# Revit family: 36-90-285-DN65-400
name_source: partatom
category: Pipe Accessories
units: mm (PartAtom-declared; Revit-internal decimal feet)

## family parameters
Always vertical = No
Cut with Voids When Loaded = No
Part Type = Valve - Breaks Into
Round Connector Dimension = Use Diameter
Shared = No
Work Plane-Based = No

## types (13) — shared parameters
Body_Wallthickness = 5 mm  [stored 0.0164042 ft]
DN 065 = Yes
DN 080 = Yes
DN 100 = Yes
DN 125 = Yes
DN 150-160 = Yes
DN 150-180 = Yes
DN 200-200 = Yes
DN 200-225 = Yes
DN 250-250 = Yes
DN 250-280 = Yes
DN 300-315 = Yes
DN 300-355 = Yes
DN 400 = Yes
DN065 = 36-075-88-701084
DN080 = 36-090-88-701084
DN100 = 36-110-88-701084
DN125 = 36-125-88-701084
DN150-160 = 36-160-88-701084
DN200-200 = 36-200-88-701084
DN200-225 = 36-225-88-701084
DN250-280 = 36-280-88-701084
DN300-315 = 36-315-88-701084
DN300-355 = 36-355-88-701084
Description_ = AVK_GATE_VALVE,PE PIPE ENDS
Name_Height_reference = 10 mm  [stored 0.0328084 ft]
Rib_Thickness = 18 mm  [stored 0.0590551 ft]
Search_table = 36-90-285-DN65-400
URL product pages = https://www.avkvalves.com
zero-valued in all types: Bottom_Reference

## per-type parameters (varying)
- DN 065: At=54.5 mm; Body_Height=115 mm; Body_Length=170 mm; Body_depth=109 mm; Body_width=60 mm; Bonnet_Flange_Depth=135 mm; Bonnet_Flange_Width=76 mm; Bonnet_Flange_cut=7.5 mm  [stored 0.0246063 ft]; Bonnet_Flange_thickness=15 mm  [stored 0.0492126 ft]; Bonnet_Height=46.5 mm; Bonnet_Reference_height=105 mm; Bonnet_Thickness=61.2 mm; Bt=61.2 mm; Bt_2=54 mm; CL _Thickness=19 mm  [stored 0.062336 ft]; CL_Height_2=59.5 mm; CL_Thickness 2=21.5 mm  [stored 0.0705381 ft]; Cut_Reference=340 mm; Cut_ref=1350 mm; D=37.5 mm  [stored 0.123031 ft]; D2=44 mm; DN150-180=36-180-88-701084; DN250-250=36-250-88-701084; DN400=36-400-88-701084; F=8.5 mm  [stored 0.0278871 ft]; F1=10 mm  [stored 0.0328084 ft]; F2=34 mm  [stored 0.111549 ft]; F_OD=51 mm; Fillet_Thickness=6 mm  [stored 0.019685 ft]; Flange_OR=39.5 mm; Flange_Thickness=19 mm  [stored 0.062336 ft]; H=271 mm; H3=322 mm; Horizontal_Flange_width=102 mm; ID=32.5 mm  [stored 0.106627 ft]; ID (Radius)=32.5 mm  [stored 0.106627 ft]; L=900 mm; L1=250 mm; L2=400 mm; L_Dia=65 mm; Length=900 mm; Name_Reference=95.833 mm; Name_Width=30 mm  [stored 0.0984252 ft]; Neck_H=62.5 mm; Neck_T=17 mm  [stored 0.0557743 ft]; Neck_T2=15 mm  [stored 0.0492126 ft]; Nominal Diameter (DN)=65 mm; R1tv=930 mm; R2f=15 mm  [stored 0.0492126 ft]; Rf=170 mm; Rib_Height_Reference_1=120 mm; Rib_Height_Reference_2=110 mm; Rib_Height_Reference_3=100 mm; Rib_Height_Reference_4=75 mm; Rib_Width_1=30 mm  [stored 0.0984252 ft]; Rib_Width_2=30 mm  [stored 0.0984252 ft]; Rib_Width_3=30 mm  [stored 0.0984252 ft]; Rib_depth_1=30 mm  [stored 0.0984252 ft]; Rib_depth_2=30 mm  [stored 0.0984252 ft]; Rib_depth_3=30 mm  [stored 0.0984252 ft]; Rt=310 mm
- DN 080: At=62.5 mm; Body_Height=136 mm; Body_Length=180 mm; Body_depth=125 mm; Body_width=72 mm; Bonnet_Flange_Depth=150 mm; Bonnet_Flange_Width=87 mm; Bonnet_Flange_cut=7.5 mm  [stored 0.0246063 ft]; Bonnet_Flange_thickness=15 mm  [stored 0.0492126 ft]; Bonnet_Height=50 mm; Bonnet_Reference_height=126 mm; Bonnet_Thickness=73.44 mm; Bt=73.44 mm; Bt_2=66 mm; CL _Thickness=25 mm  [stored 0.082021 ft]; CL_Height_2=67.5 mm; CL_Thickness 2=27.5 mm  [stored 0.0902231 ft]; Cut_Reference=360 mm; Cut_ref=1350 mm; D=45 mm; D2=50 mm; DN150-180=36-180-88-701084; DN250-250=36-250-88-701084; DN400=36-400-88-701084; F=8.5 mm  [stored 0.0278871 ft]; F1=10 mm  [stored 0.0328084 ft]; F2=34 mm  [stored 0.111549 ft]; F_OD=54 mm; Fillet_Thickness=6 mm  [stored 0.019685 ft]; Flange_OR=47.5 mm; Flange_Thickness=19 mm  [stored 0.062336 ft]; H=297 mm; H3=351 mm; Horizontal_Flange_width=108 mm; ID=40 mm; ID (Radius)=40 mm; L=900 mm; L1=255 mm; L2=390 mm; L_Dia=80 mm; Length=900 mm; Name_Reference=113.333 mm; Name_Width=36 mm  [stored 0.11811 ft]; Neck_H=59.5 mm; Neck_T=23 mm  [stored 0.0754593 ft]; Neck_T2=21 mm; Nominal Diameter (DN)=80 mm; R1tv=1000 mm; R2f=15 mm  [stored 0.0492126 ft]; Rf=180 mm; Rib_Height_Reference_1=120 mm; Rib_Height_Reference_2=110 mm; Rib_Height_Reference_3=100 mm; Rib_Height_Reference_4=85 mm; Rib_Width_1=36 mm  [stored 0.11811 ft]; Rib_Width_2=36 mm  [stored 0.11811 ft]; Rib_Width_3=36 mm  [stored 0.11811 ft]; Rib_depth_1=36 mm  [stored 0.11811 ft]; Rib_depth_2=36 mm  [stored 0.11811 ft]; Rib_depth_3=36 mm  [stored 0.11811 ft]; Rt=333.333 mm
- DN 100: At=77.5 mm; Body_Height=148 mm; Body_Length=190 mm; Body_depth=155 mm; Body_width=81 mm; Bonnet_Flange_Depth=180 mm; Bonnet_Flange_Width=112 mm; Bonnet_Flange_cut=7.5 mm  [stored 0.0246063 ft]; Bonnet_Flange_thickness=15 mm  [stored 0.0492126 ft]; Bonnet_Height=55 mm; Bonnet_Reference_height=138 mm; Bonnet_Thickness=82.62 mm; Bt=82.62 mm; Bt_2=75 mm; CL _Thickness=29.5 mm  [stored 0.0967848 ft]; CL_Height_2=82.5 mm; CL_Thickness 2=32 mm  [stored 0.104987 ft]; Cut_Reference=380 mm; Cut_ref=1290 mm; D=55 mm; D2=64 mm; DN150-180=36-180-88-701084; DN250-250=36-250-88-701084; DN400=36-400-88-701084; F=9.5 mm  [stored 0.031168 ft]; F1=11 mm  [stored 0.0360892 ft]; F2=38 mm  [stored 0.124672 ft]; F_OD=67 mm; Fillet_Thickness=6 mm  [stored 0.019685 ft]; Flange_OR=57.5 mm; Flange_Thickness=100 mm; H=334 mm; H3=401 mm; Horizontal_Flange_width=134 mm; ID=50 mm; ID (Radius)=50 mm; L=860 mm; L1=265 mm; L2=330 mm; L_Dia=100 mm; Length=860 mm; Name_Reference=123.333 mm; Name_Width=40.5 mm; Neck_H=65.5 mm; Neck_T=27.5 mm  [stored 0.0902231 ft]; Neck_T2=25.5 mm  [stored 0.0836614 ft]; Nominal Diameter (DN)=100 mm; R1tv=1100 mm; R2f=15 mm  [stored 0.0492126 ft]; Rf=223.333 mm; Rib_Height_Reference_1=120 mm; Rib_Height_Reference_2=110 mm; Rib_Height_Reference_3=100 mm; Rib_Height_Reference_4=90 mm; Rib_Width_1=40.5 mm; Rib_Width_2=40.5 mm; Rib_Width_3=40.5 mm; Rib_depth_1=40.5 mm; Rib_depth_2=40.5 mm; Rib_depth_3=40.5 mm; Rt=366.667 mm
- DN 150-160: At=113 mm; Body_Height=205 mm; Body_Length=191 mm; Body_depth=226 mm; Body_width=96 mm; Bonnet_Flange_Depth=250 mm; Bonnet_Flange_Width=130 mm; Bonnet_Flange_cut=7.5 mm  [stored 0.0246063 ft]; Bonnet_Flange_thickness=15 mm  [stored 0.0492126 ft]; Bonnet_Height=71 mm; Bonnet_Reference_height=195 mm; Bonnet_Thickness=97.92 mm; Bt=97.92 mm; Bt_2=90 mm; CL _Thickness=34 mm  [stored 0.111549 ft]; CL_Height_2=118 mm; CL_Thickness 2=36.5 mm  [stored 0.119751 ft]; Cut_Reference=382 mm; Cut_ref=1605 mm; D=80 mm; D2=83 mm; DN150-180=36-180-88-701084; DN250-250=36-250-88-701084; DN400=36-400-88-701084
36-400-88-701084; F=9.5 mm  [stored 0.031168 ft]; F1=11 mm  [stored 0.0360892 ft]; F2=38 mm  [stored 0.124672 ft]; F_OD=97 mm; Fillet_Thickness=12 mm  [stored 0.0393701 ft]; Flange_OR=77.5 mm; Flange_Thickness=19 mm  [stored 0.062336 ft]; H=448 mm; H3=545 mm; Horizontal_Flange_width=194 mm; ID=75 mm; ID (Radius)=75.08 mm; L=1070 mm; L1=265 mm; L2=540 mm; L_Dia=150.16 mm; Length=1070 mm; Name_Reference=170.833 mm; Name_Width=48 mm; Neck_H=87 mm; Neck_T=32 mm  [stored 0.104987 ft]; Neck_T2=30 mm  [stored 0.0984252 ft]; Nominal Diameter (DN)=150.16 mm; R1tv=1420 mm; R2f=30 mm  [stored 0.0984252 ft]; Rf=323.333 mm; Rib_Height_Reference_1=120 mm; Rib_Height_Reference_2=110 mm; Rib_Height_Reference_3=100 mm; Rib_Height_Reference_4=150 mm; Rib_Width_1=48 mm; Rib_Width_2=48 mm; Rib_Width_3=48 mm; Rib_depth_1=48 mm; Rib_depth_2=48 mm; Rib_depth_3=48 mm; Rt=473.333 mm
- DN 200-200: At=128.5 mm; Body_Height=289 mm; Body_Length=200 mm; Body_depth=257 mm; Body_width=116 mm; Bonnet_Flange_Depth=283 mm; Bonnet_Flange_Width=150 mm; Bonnet_Flange_cut=12.5 mm  [stored 0.0410105 ft]; Bonnet_Flange_thickness=25 mm  [stored 0.082021 ft]; Bonnet_Height=85 mm; Bonnet_Reference_height=279 mm; Bonnet_Thickness=118.32 mm; Bt=118.32 mm; Bt_2=110 mm; CL _Thickness=38 mm  [stored 0.124672 ft]; CL_Height_2=133.5 mm; CL_Thickness 2=40.5 mm; Cut_Reference=400 mm; Cut_ref=1500 mm; D=100 mm; D2=106 mm; DN150-180=36-180-88-701084; DN250-250=36-250-88-701084; DN400=36-400-88-701084; F=12 mm  [stored 0.0393701 ft]; F1=13.5 mm  [stored 0.0442913 ft]; F2=42 mm; F_OD=115 mm; Fillet_Thickness=24 mm  [stored 0.0787402 ft]; Flange_OR=110 mm; Flange_Thickness=20 mm  [stored 0.0656168 ft]; H=562 mm; H3=677 mm; Horizontal_Flange_width=230 mm; ID=90 mm; ID (Radius)=100.1 mm; L=1000 mm; L1=300 mm; L2=400 mm; L_Dia=200.2 mm; Length=1000 mm; Name_Reference=240.833 mm; Name_Width=58 mm; Neck_H=97.5 mm; Neck_T=36 mm  [stored 0.11811 ft]; Neck_T2=34 mm  [stored 0.111549 ft]; Nominal Diameter (DN)=200.2 mm; R1tv=1700 mm; R2f=60 mm; Rf=383.333 mm; Rib_Height_Reference_1=120 mm; Rib_Height_Reference_2=110 mm; Rib_Height_Reference_3=100 mm; Rib_Height_Reference_4=180 mm; Rib_Width_1=58 mm; Rib_Width_2=58 mm; Rib_Width_3=58 mm; Rib_depth_1=58 mm; Rib_depth_2=58 mm; Rib_depth_3=58 mm; Rt=566.667 mm
- DN 250-250: At=164.5 mm; Body_Height=305 mm; Body_Length=242 mm; Body_depth=329 mm; Body_width=112 mm; Bonnet_Flange_Depth=372 mm; Bonnet_Flange_Width=144 mm; Bonnet_Flange_cut=12.5 mm  [stored 0.0410105 ft]; Bonnet_Flange_thickness=25 mm  [stored 0.082021 ft]; Bonnet_Height=97.5 mm; Bonnet_Reference_height=295 mm; Bonnet_Thickness=114.24 mm; Bt=114.24 mm; Bt_2=106 mm; CL _Thickness=36 mm  [stored 0.11811 ft]; CL_Height_2=169.5 mm; CL_Thickness 2=38.5 mm; Cut_Reference=484 mm; Cut_ref=1920 mm; D=125 mm; D2=109 mm; DN150-180=36-200-88-701084; DN250-250=36-250-88-701084; DN400=36-400-88-701084; F=13.5 mm  [stored 0.0442913 ft]; F1=15.5 mm  [stored 0.050853 ft]; F2=47 mm; F_OD=146 mm; Fillet_Thickness=24 mm  [stored 0.0787402 ft]; Flange_OR=127.5 mm; Flange_Thickness=22 mm  [stored 0.0721785 ft]; H=664 mm; H3=810 mm; Horizontal_Flange_width=292 mm; ID=115 mm; ID (Radius)=125.125 mm; L=1280 mm; L1=270 mm; L2=740 mm; L_Dia=250.25 mm; Length=1280 mm; Name_Reference=254.167 mm; Name_Width=56 mm; Neck_H=142.5 mm; Neck_T=34 mm  [stored 0.111549 ft]; Neck_T2=32 mm  [stored 0.104987 ft]; Nominal Diameter (DN)=250.25 mm; R1tv=1950 mm; R2f=60 mm; Rf=486.667 mm; Rib_Height_Reference_1=90 mm; Rib_Height_Reference_2=110 mm; Rib_Height_Reference_3=100 mm; Rib_Height_Reference_4=200 mm; Rib_Width_1=126 mm; Rib_Width_2=56 mm; Rib_Width_3=56 mm; Rib_depth_1=385 mm; Rib_depth_2=56 mm; Rib_depth_3=56 mm; Rt=650 mm
- DN 300-315: At=209 mm; Body_Height=370 mm; Body_Length=284 mm; Body_depth=418 mm; Body_width=129 mm; Bonnet_Flange_Depth=448 mm; Bonnet_Flange_Width=172 mm; Bonnet_Flange_cut=17.5 mm  [stored 0.0574147 ft]; Bonnet_Flange_thickness=35 mm  [stored 0.114829 ft]; Bonnet_Height=114 mm; Bonnet_Reference_height=360 mm; Bonnet_Thickness=131.58 mm; Bt=131.58 mm; Bt_2=123 mm; CL _Thickness=44.5 mm; CL_Height_2=214 mm; CL_Thickness 2=47 mm; Cut_Reference=568 mm; Cut_ref=2130 mm; D=157.5 mm; D2=110 mm; DN150-180=36-180-88-701084; DN250-250=36-250-88-701084; DN400=36-400-88-701084; F=13.5 mm  [stored 0.0442913 ft]; F1=15.5 mm  [stored 0.050853 ft]; F2=47 mm; F_OD=184 mm; Fillet_Thickness=24 mm  [stored 0.0787402 ft]; Flange_OR=161 mm; Flange_Thickness=24.5 mm  [stored 0.0803806 ft]; H=740 mm; H3=924 mm; Horizontal_Flange_width=368 mm; ID=150 mm; ID (Radius)=150.158 mm; L=1420 mm; L1=265 mm; L2=890 mm; L_Dia=300.315 mm; Length=1420 mm; Name_Reference=308.333 mm; Name_Width=64.5 mm; Neck_H=109 mm; Neck_T=42.5 mm; Neck_T2=40.5 mm; Nominal Diameter (DN)=300.315 mm; R1tv=2280 mm; R2f=60 mm; Rf=613.333 mm; Rib_Height_Reference_1=240 mm; Rib_Height_Reference_2=285 mm; Rib_Height_Reference_3=130 mm; Rib_Height_Reference_4=260 mm; Rib_Width_1=155 mm; Rib_Width_2=155 mm; Rib_Width_3=64.5 mm; Rib_depth_1=456 mm; Rib_depth_2=456 mm; Rib_depth_3=64.5 mm; Rt=760 mm
- DN 400: At=238 mm; Body_Height=485 mm; Body_Length=290 mm; Body_depth=476 mm; Body_width=150 mm; Bonnet_Flange_Depth=554 mm; Bonnet_Flange_Width=178 mm; Bonnet_Flange_cut=35 mm  [stored 0.114829 ft]; Bonnet_Flange_thickness=70 mm; Bonnet_Height=145 mm; Bonnet_Reference_height=475 mm; Bonnet_Thickness=153 mm; Bt=153 mm; Bt_2=144 mm; CL _Thickness=51 mm; CL_Height_2=243 mm; CL_Thickness 2=53.5 mm; Cut_Reference=580 mm; Cut_ref=2550 mm; D=200 mm; D2=52 mm; DN150-180=36-180-88-701084; DN250-250=36-250-88-701084; DN400=36-400-88-701084; F=16 mm  [stored 0.0524934 ft]; F1=18.5 mm  [stored 0.0606955 ft]; F2=55 mm; F_OD=253 mm; Fillet_Thickness=32 mm  [stored 0.104987 ft]; Flange_OR=212 mm; Flange_Thickness=28 mm  [stored 0.0918635 ft]; H=912 mm; H3=1165 mm; Horizontal_Flange_width=506 mm; ID=190 mm; ID (Radius)=200 mm; L=1700 mm; L1=355 mm; L2=990 mm; L_Dia=400 mm; Length=1700 mm; Name_Reference=404.167 mm; Name_Width=75 mm; Neck_H=129 mm; Neck_T=49 mm; Neck_T2=47 mm; Nominal Diameter (DN)=400 mm; R1tv=2900 mm; R2f=80 mm; Rf=843.333 mm; Rib_Height_Reference_1=81 mm; Rib_Height_Reference_2=210 mm; Rib_Height_Reference_3=330 mm; Rib_Height_Reference_4=440 mm; Rib_Width_1=146 mm; Rib_Width_2=146 mm; Rib_Width_3=146 mm; Rib_depth_1=564 mm; Rib_depth_2=564 mm; Rib_depth_3=564 mm; Rt=966.667 mm
- DN 125: At=108.5 mm; Body_Height=170 mm; Body_Length=166 mm; Body_depth=217 mm; Body_width=68 mm; Bonnet_Flange_Depth=235 mm; Bonnet_Flange_Width=98 mm; Bonnet_Flange_cut=7.5 mm  [stored 0.0246063 ft]; Bonnet_Flange_thickness=15 mm  [stored 0.0492126 ft]; Bonnet_Height=62.5 mm; Bonnet_Reference_height=160 mm; Bonnet_Thickness=69.36 mm; Bt=69.36 mm; Bt_2=62 mm; CL _Thickness=23 mm  [stored 0.0754593 ft]; CL_Height_2=113.5 mm; CL_Thickness 2=25.5 mm  [stored 0.0836614 ft]; Cut_Reference=332 mm; Cut_ref=1335 mm; D=62.5 mm; D2=65 mm; DN150-180=36-180-88-701084; DN250-250=36-250-88-701084; DN400=36-400-88-701084; F=9.5 mm  [stored 0.031168 ft]; F1=11 mm  [stored 0.0360892 ft]; F2=38 mm  [stored 0.124672 ft]; F_OD=76 mm; Fillet_Thickness=6 mm  [stored 0.019685 ft]; Flange_OR=70.5 mm; Flange_Thickness=120 mm; H=376 mm; H3=452 mm; Horizontal_Flange_width=152 mm; ID=52.5 mm; ID (Radius)=62.5 mm; L=890 mm; L1=300 mm; L2=290 mm; L_Dia=125 mm; Length=890 mm; Name_Reference=141.667 mm; Name_Width=34 mm  [stored 0.111549 ft]; Neck_H=54.5 mm; Neck_T=21 mm; Neck_T2=19 mm  [stored 0.062336 ft]; Nominal Diameter (DN)=125 mm; R1tv=1250 mm; R2f=15 mm  [stored 0.0492126 ft]; Rf=253.333 mm; Rib_Height_Reference_1=120 mm; Rib_Height_Reference_2=110 mm; Rib_Height_Reference_3=100 mm; Rib_Height_Reference_4=120 mm; Rib_Width_1=34 mm  [stored 0.111549 ft]; Rib_Width_2=34 mm  [stored 0.111549 ft]; Rib_Width_3=34 mm  [stored 0.111549 ft]; Rib_depth_1=34 mm  [stored 0.111549 ft]; Rib_depth_2=34 mm  [stored 0.111549 ft]; Rib_depth_3=34 mm  [stored 0.111549 ft]; Rt=416.667 mm
- DN 300-355: At=209 mm; Body_Height=370 mm; Body_Length=284 mm; Body_depth=418 mm; Body_width=129 mm; Bonnet_Flange_Depth=448 mm; Bonnet_Flange_Width=172 mm; Bonnet_Flange_cut=17.5 mm  [stored 0.0574147 ft]; Bonnet_Flange_thickness=35 mm  [stored 0.114829 ft]; Bonnet_Height=114 mm; Bonnet_Reference_height=360 mm; Bonnet_Thickness=131.58 mm; Bt=131.58 mm; Bt_2=123 mm; CL _Thickness=44.5 mm; CL_Height_2=214 mm; CL_Thickness 2=47 mm; Cut_Reference=568 mm; Cut_ref=2280 mm; D=177.5 mm; D2=110 mm; DN150-180=36-180-88-701084; DN250-250=36-225-88-701084; DN400=36-400-88-701084; F=13.5 mm  [stored 0.0442913 ft]; F1=15.5 mm  [stored 0.050853 ft]; F2=47 mm; F_OD=221 mm; Fillet_Thickness=24 mm  [stored 0.0787402 ft]; Flange_OR=161 mm; Flange_Thickness=24.5 mm  [stored 0.0803806 ft]; H=740 mm; H3=961 mm; Horizontal_Flange_width=442 mm; ID=150 mm; ID (Radius)=150.178 mm; L=1520 mm; L1=355 mm; L2=810 mm; L_Dia=300.355 mm; Length=1520 mm; Name_Reference=308.333 mm; Name_Width=64.5 mm; Neck_H=109 mm; Neck_T=42.5 mm; Neck_T2=40.5 mm; Nominal Diameter (DN)=300.355 mm; R1tv=2280 mm; R2f=60 mm; Rf=736.667 mm; Rib_Height_Reference_1=240 mm; Rib_Height_Reference_2=285 mm; Rib_Height_Reference_3=130 mm; Rib_Height_Reference_4=260 mm; Rib_Width_1=155 mm; Rib_Width_2=155 mm; Rib_Width_3=64.5 mm; Rib_depth_1=456 mm; Rib_depth_2=456 mm; Rib_depth_3=64.5 mm; Rt=760 mm
- DN 250-280: At=164.5 mm; Body_Height=305 mm; Body_Length=242 mm; Body_depth=329 mm; Body_width=112 mm; Bonnet_Flange_Depth=372 mm; Bonnet_Flange_Width=144 mm; Bonnet_Flange_cut=12.5 mm  [stored 0.0410105 ft]; Bonnet_Flange_thickness=25 mm  [stored 0.082021 ft]; Bonnet_Height=97.5 mm; Bonnet_Reference_height=295 mm; Bonnet_Thickness=114.24 mm; Bt=114.24 mm; Bt_2=106 mm; CL _Thickness=36 mm  [stored 0.11811 ft]; CL_Height_2=169.5 mm; CL_Thickness 2=38.5 mm; Cut_Reference=484 mm; Cut_ref=2040 mm; D=140 mm; D2=109 mm; DN150-180=36-180-88-701084; DN250-250=36-250-88-701084; DN400=36-400-88-701084; F=13.5 mm  [stored 0.0442913 ft]; F1=15.5 mm  [stored 0.050853 ft]; F2=47 mm; F_OD=159 mm; Fillet_Thickness=24 mm  [stored 0.0787402 ft]; Flange_OR=127.5 mm; Flange_Thickness=22 mm  [stored 0.0721785 ft]; H=664 mm; H3=823 mm; Horizontal_Flange_width=318 mm; ID=125 mm; ID (Radius)=125.14 mm; L=1360 mm; L1=365 mm; L2=630 mm; L_Dia=250.28 mm; Length=1360 mm; Name_Reference=254.167 mm; Name_Width=56 mm; Neck_H=142.5 mm; Neck_T=34 mm  [stored 0.111549 ft]; Neck_T2=32 mm  [stored 0.104987 ft]; Nominal Diameter (DN)=250.28 mm; R1tv=1950 mm; R2f=60 mm; Rf=530 mm; Rib_Height_Reference_1=90 mm; Rib_Height_Reference_2=110 mm; Rib_Height_Reference_3=100 mm; Rib_Height_Reference_4=200 mm; Rib_Width_1=126 mm; Rib_Width_2=56 mm; Rib_Width_3=56 mm; Rib_depth_1=385 mm; Rib_depth_2=56 mm; Rib_depth_3=56 mm; Rt=650 mm
- DN 200-225: At=128.5 mm; Body_Height=289 mm; Body_Length=200 mm; Body_depth=257 mm; Body_width=116 mm; Bonnet_Flange_Depth=283 mm; Bonnet_Flange_Width=150 mm; Bonnet_Flange_cut=12.5 mm  [stored 0.0410105 ft]; Bonnet_Flange_thickness=25 mm  [stored 0.082021 ft]; Bonnet_Height=85 mm; Bonnet_Reference_height=279 mm; Bonnet_Thickness=118.32 mm; Bt=118.32 mm; Bt_2=110 mm; CL _Thickness=38 mm  [stored 0.124672 ft]; CL_Height_2=133.5 mm; CL_Thickness 2=40.5 mm; Cut_Reference=400 mm; Cut_ref=1650 mm; D=112.5 mm; D2=106 mm; DN150-180=36-180-88-701084; DN250-250=36-250-88-701084; DN400=36-400-88-701084; F=12 mm  [stored 0.0393701 ft]; F1=13.5 mm  [stored 0.0442913 ft]; F2=42 mm; F_OD=134 mm; Fillet_Thickness=24 mm  [stored 0.0787402 ft]; Flange_OR=110 mm; Flange_Thickness=20 mm  [stored 0.0656168 ft]; H=562 mm; H3=696 mm; Horizontal_Flange_width=268 mm; ID=100 mm; ID (Radius)=100.113 mm; L=1100 mm; L1=265 mm; L2=570 mm; L_Dia=200.225 mm; Length=1100 mm; Name_Reference=240.833 mm; Name_Width=58 mm; Neck_H=97.5 mm; Neck_T=36 mm  [stored 0.11811 ft]; Neck_T2=34 mm  [stored 0.111549 ft]; Nominal Diameter (DN)=200.225 mm; R1tv=1700 mm; R2f=60 mm; Rf=446.667 mm; Rib_Height_Reference_1=120 mm; Rib_Height_Reference_2=110 mm; Rib_Height_Reference_3=100 mm; Rib_Height_Reference_4=180 mm; Rib_Width_1=58 mm; Rib_Width_2=58 mm; Rib_Width_3=58 mm; Rib_depth_1=58 mm; Rib_depth_2=58 mm; Rib_depth_3=58 mm; Rt=566.667 mm
- DN 150-180: At=113 mm; Body_Height=205 mm; Body_Length=191 mm; Body_depth=226 mm; Body_width=96 mm; Bonnet_Flange_Depth=250 mm; Bonnet_Flange_Width=130 mm; Bonnet_Flange_cut=7.5 mm  [stored 0.0246063 ft]; Bonnet_Flange_thickness=15 mm  [stored 0.0492126 ft]; Bonnet_Height=71 mm; Bonnet_Reference_height=195 mm; Bonnet_Thickness=97.92 mm; Bt=97.92 mm; Bt_2=90 mm; CL _Thickness=34 mm  [stored 0.111549 ft]; CL_Height_2=118 mm; CL_Thickness 2=36.5 mm  [stored 0.119751 ft]; Cut_Reference=382 mm; Cut_ref=1605 mm; D=90 mm; D2=83 mm; DN150-180=36-180-88-701084; DN250-250=36-250-88-701084; DN400=36-400-88-701084; F=9.5 mm  [stored 0.031168 ft]; F1=11 mm  [stored 0.0360892 ft]; F2=38 mm  [stored 0.124672 ft]; F_OD=102 mm; Fillet_Thickness=12 mm  [stored 0.0393701 ft]; Flange_OR=77.5 mm; Flange_Thickness=19 mm  [stored 0.062336 ft]; H=448 mm; H3=550 mm; Horizontal_Flange_width=204 mm; ID=75 mm; ID (Radius)=75.09 mm; L=1070 mm; L1=265 mm; L2=540 mm; L_Dia=150.18 mm; Length=1070 mm; Name_Reference=170.833 mm; Name_Width=48 mm; Neck_H=87 mm; Neck_T=32 mm  [stored 0.104987 ft]; Neck_T2=30 mm  [stored 0.0984252 ft]; Nominal Diameter (DN)=150.18 mm; R1tv=1420 mm; R2f=30 mm  [stored 0.0984252 ft]; Rf=340 mm; Rib_Height_Reference_1=120 mm; Rib_Height_Reference_2=110 mm; Rib_Height_Reference_3=100 mm; Rib_Height_Reference_4=150 mm; Rib_Width_1=48 mm; Rib_Width_2=48 mm; Rib_Width_3=48 mm; Rib_depth_1=48 mm; Rib_depth_2=48 mm; Rib_depth_3=48 mm; Rt=473.333 mm

note: [stored X ft] marks values corroborated as IEEE doubles in the binary element streams (Revit-internal decimal feet)

## geometry (parser evidence)
native form markers: Extrusion x1, Sweep x3
no freeform markers — native parametric forms only
